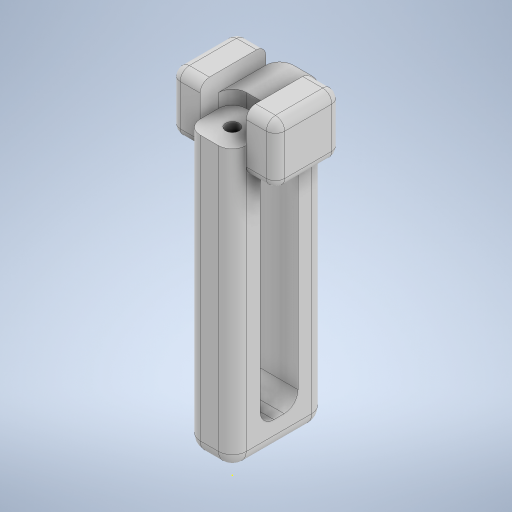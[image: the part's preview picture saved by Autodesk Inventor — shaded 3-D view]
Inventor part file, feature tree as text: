
AUTODESK INVENTOR PART (.ipt)
format: ipt  version: 2023 (Build 270158000, 158)  size: 405,504 bytes
history: native  units: in
note: dims shown in document units (in); Inventor stores cm internally (conversion verified against a paired STEP export)
features: sketch x8, extrude x7, fillet x4, projected_geometry x2, plane x1
ambient origin geometry x8: Origin, YZ Plane, XZ Plane, XY Plane, X Axis, Y Axis, Z Axis, Center Point
bodies: Solid1 (feature_tree)
feature tree (22):
  extrude  "Extrusion1"  Depth=0.797in
  fillet  "Fillet1"  Radius=2.5in
  extrude  "Extrusion2"  Depth=0.3937in
  extrude  "Extrusion3"  Depth=0.1181in TaperAngle=0.0deg
  sketch  "Sketch4"  dims[d14=0.1161in d15=0.3937in d16=0.0in]
  extrude  "Extrusion4"  Depth=0.3937in TaperAngle=0.0deg
  plane  "Work Plane4"
  extrude  "Extrusion6"  Depth=0.1181in TaperAngle=0.0deg
  extrude  "Extrusion7"  Depth=0.25in
  fillet  "Fillet3"  Radius=0.1575in
  extrude  "Extrusion8"  Depth=0.25in TaperAngle=0.0deg
  fillet  "Fillet4"  Radius=0.0787in
  fillet  "Fillet5"  Radius=0.2362in
  sketch  "Sketch1"  dims[d0=0.3937in d1=0.797in d2=2.5in d3=0.0in]
  sketch  "Sketch2"  dims[d4=0.1181in d8=0.3937in]
  sketch  "Sketch3"  dims[d10=0.1181in d11=0.1181in d12=0.0in]
  sketch  "Sketch5"  dims[d18=0.1181in d19=2.0in d20=0.0in]
  sketch  "Sketch6"  dims[d22=0.1181in d24=0.25in d27=0.1575in d28=0.0in]
  sketch  "Sketch7"  dims[d29=0.271in d30=0.25in d31=0.0in d32=0.0787in d33=0.2362in]
  sketch  "Sketch8"  dims[d34=0.25in d35=0.0in d36=0.0787in d37=0.5in d38=0.0in d39=0.0787in d6=0.5in d7=0.0344in d9=0.0344in d25=0.0197in d26=0.0344in d40=0.0in d41=0.0in d42=0.0in]
  projected_geometry  "Project Cut Edges1"
  projected_geometry  "Project Cut Edges2"
